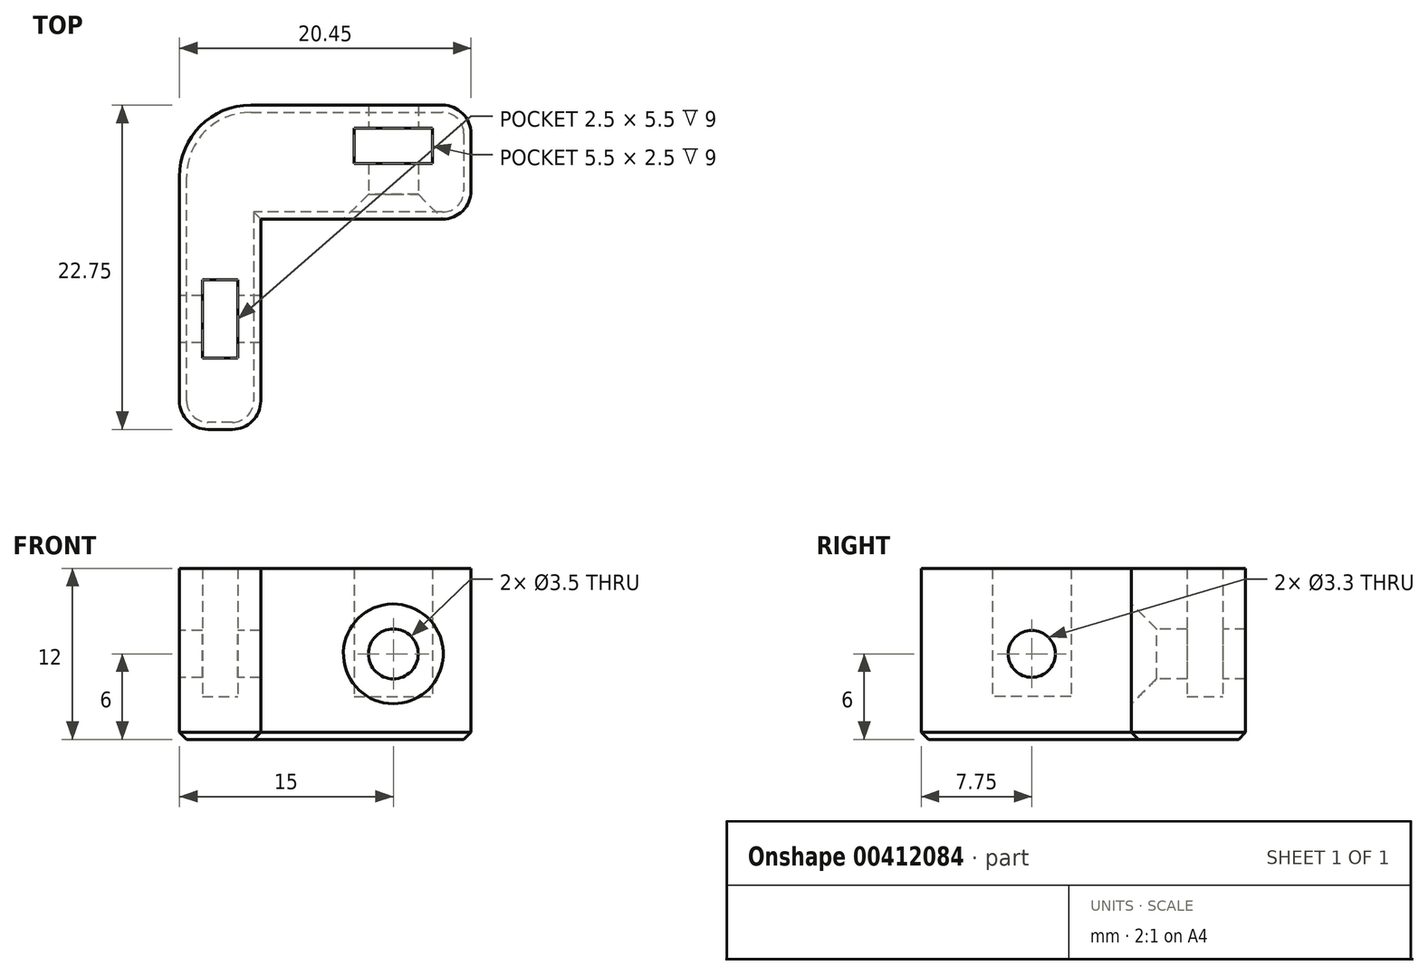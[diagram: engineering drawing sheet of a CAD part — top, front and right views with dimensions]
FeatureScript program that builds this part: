
annotation { "Feature Type Name" : "Feature", "Feature Type Description" : "" }
export const myFeature = defineFeature(function(context is Context, id is Id, definition is map)
    precondition{}
    {
        {
            var Q0;
            Q0=qCreatedBy(makeId("Top.planeOp"),FACE);
            var sketch = newSketch(context, id + "F0", { "sketchPlane" : qUnion([Q0])});
            skLineSegment(sketch, "E0", {"start": v(-15, -7.75) * mm, "end": v(-15, 15) * mm});
            skLineSegment(sketch, "E1", {"start": v(-15, 15) * mm, "end": v(5.45, 15) * mm});
            skLineSegment(sketch, "E2", {"start": v(5.45, 15) * mm, "end": v(5.45, 7) * mm});
            skLineSegment(sketch, "E3", {"start": v(5.45, 7) * mm, "end": v(-9.3, 7) * mm});
            skLineSegment(sketch, "E4", {"start": v(-9.3, 7) * mm, "end": v(-9.3, -7.75) * mm});
            skLineSegment(sketch, "E5", {"start": v(-9.3, -7.75) * mm, "end": v(-15, -7.75) * mm});
            skLineSegment(sketch, "E6.bottom", {"start": v(-13.4, 2.75) * mm, "end": v(-10.9, 2.75) * mm});
            skLineSegment(sketch, "E6.top", {"start": v(-13.4, -2.75) * mm, "end": v(-10.9, -2.75) * mm});
            skLineSegment(sketch, "E6.left", {"start": v(-13.4, 2.75) * mm, "end": v(-13.4, -2.75) * mm});
            skLineSegment(sketch, "E6.right", {"start": v(-10.9, 2.75) * mm, "end": v(-10.9, -2.75) * mm});
            skLineSegment(sketch, "E7.bottom", {"start": v(-2.75, 10.9) * mm, "end": v(2.75, 10.9) * mm});
            skLineSegment(sketch, "E7.top", {"start": v(-2.75, 13.4) * mm, "end": v(2.75, 13.4) * mm});
            skLineSegment(sketch, "E7.left", {"start": v(-2.75, 10.9) * mm, "end": v(-2.75, 13.4) * mm});
            skLineSegment(sketch, "E7.right", {"start": v(2.75, 10.9) * mm, "end": v(2.75, 13.4) * mm});
            skLineSegment(sketch, "E8", {"start": v(-10.9, 2.75) * mm, "end": v(-2.75, 10.9) * mm, "construction": true});
            skLineSegment(sketch, "E9.bottom", {"start": v(-15, 15) * mm, "end": v(-21, 15) * mm, "construction": true});
            skLineSegment(sketch, "E9.top", {"start": v(-15, -17.94) * mm, "end": v(-21, -17.94) * mm, "construction": true});
            skLineSegment(sketch, "E9.left", {"start": v(-15, 15) * mm, "end": v(-15, -17.94) * mm, "construction": true});
            skLineSegment(sketch, "E9.right", {"start": v(-21, 15) * mm, "end": v(-21, -17.94) * mm, "construction": true});
            skLineSegment(sketch, "E10.bottom", {"start": v(-21, 15) * mm, "end": v(24.07, 15) * mm, "construction": true});
            skLineSegment(sketch, "E10.top", {"start": v(-21, 21) * mm, "end": v(24.07, 21) * mm, "construction": true});
            skLineSegment(sketch, "E10.left", {"start": v(-21, 15) * mm, "end": v(-21, 21) * mm, "construction": true});
            skLineSegment(sketch, "E10.right", {"start": v(24.07, 15) * mm, "end": v(24.07, 21) * mm, "construction": true});
            skLineSegment(sketch, "E11", {"start": v(-9.3, -7.75) * mm, "end": v(5.45, 7) * mm, "construction": true});
            skSolve(sketch);
        }
        {
            var Q0;
            Q0=makeQuery(id+"F0.imprint","IMPRINT",FACE,{"disambiguationData":[TD([[makeQuery(id+"F0.imprint","IMPRINT",EDGE,{"derivedFrom":sQuery(id+"F0.wireOp",EDGE,"E0")}),-1.0]])]});
            extrude(context, id + "F1", {"entities" : qUnion([Q0]), "depth" : 6 * mm, "hasSecondDirection" : true, "secondDirectionOppositeDirection" : true, "secondDirectionDepth" : 6 * mm});
        }
        {
            var Q0;
            Q0=makeQuery(id+"F1.opExtrude","CAP_FACE",FACE,{"disambiguationData":[OSD([sQuery(id+"F0.wireOp",EDGE,"E0"),sQuery(id+"F0.wireOp",EDGE,"E1"),sQuery(id+"F0.wireOp",EDGE,"E2"),sQuery(id+"F0.wireOp",EDGE,"E3"),sQuery(id+"F0.wireOp",EDGE,"E4"),sQuery(id+"F0.wireOp",EDGE,"E5"),sQuery(id+"F0.wireOp",EDGE,"E6.bottom"),sQuery(id+"F0.wireOp",EDGE,"E6.top"),sQuery(id+"F0.wireOp",EDGE,"E6.left"),sQuery(id+"F0.wireOp",EDGE,"E6.right"),sQuery(id+"F0.wireOp",EDGE,"E7.bottom"),sQuery(id+"F0.wireOp",EDGE,"E7.top"),sQuery(id+"F0.wireOp",EDGE,"E7.left"),sQuery(id+"F0.wireOp",EDGE,"E7.right")])],"isStart":true});
            var sketch = newSketch(context, id + "F2", { "sketchPlane" : qUnion([Q0])});
            skSolve(sketch);
        }
        {
            var Q0;
            Q0=makeQuery(id+"F2.imprint","IMPRINT",FACE,{"disambiguationData":[TD([[makeQuery(id+"F2.imprint","IMPRINT",EDGE,{"derivedFrom":makeQuery(id+"F1.opExtrude","CAP_EDGE",EDGE,{"disambiguationData":[OSD([sQuery(id+"F0.wireOp",EDGE,"E6.bottom")])],"isStart":true})}),1.0]])]});
            var Q1;
            Q1=makeQuery(id+"F2.imprint","IMPRINT",FACE,{"disambiguationData":[TD([[makeQuery(id+"F2.imprint","IMPRINT",EDGE,{"derivedFrom":makeQuery(id+"F1.opExtrude","CAP_EDGE",EDGE,{"disambiguationData":[OSD([sQuery(id+"F0.wireOp",EDGE,"E7.bottom")])],"isStart":true})}),-1.0]])]});
            extrude(context, id + "F3", {"entities" : qUnion([Q0, Q1]), "operationType" : NewBodyOperationType.ADD, "oppositeDirection" : true, "depth" : 3 * mm});
        }
        {
            var Q0;
            Q0=makeQuery(id+"F1.opExtrude","SWEPT_FACE",FACE,{"disambiguationData":[OSD([sQuery(id+"F0.wireOp",EDGE,"E0")])]});
            var sketch = newSketch(context, id + "F4", { "sketchPlane" : qUnion([Q0])});
            skPoint(sketch, "E12", {"position": v(0, 0) * mm});
            skSolve(sketch);
        }
        {
            var Q0;
            Q0=makeQuery(id+"F1.opExtrude","SWEPT_FACE",FACE,{"disambiguationData":[OSD([sQuery(id+"F0.wireOp",EDGE,"E3")])]});
            var sketch = newSketch(context, id + "F5", { "sketchPlane" : qUnion([Q0])});
            skPoint(sketch, "E13", {"position": v(0, 0) * mm});
            skSolve(sketch);
        }
        {
            var Q0;
            Q0=sQuery(id+"F4.wireOp",VERTEX,"E12");
            var Q1;
            Q1=makeQuery(id+"F1.opExtrude","SWEPT_BODY",BODY,{"disambiguationData":[OSD([sQuery(id+"F0.wireOp",EDGE,"E0"),sQuery(id+"F0.wireOp",EDGE,"E1"),sQuery(id+"F0.wireOp",EDGE,"E2"),sQuery(id+"F0.wireOp",EDGE,"E3"),sQuery(id+"F0.wireOp",EDGE,"E4"),sQuery(id+"F0.wireOp",EDGE,"E5"),sQuery(id+"F0.wireOp",EDGE,"E6.bottom"),sQuery(id+"F0.wireOp",EDGE,"E6.top"),sQuery(id+"F0.wireOp",EDGE,"E6.left"),sQuery(id+"F0.wireOp",EDGE,"E6.right"),sQuery(id+"F0.wireOp",EDGE,"E7.bottom"),sQuery(id+"F0.wireOp",EDGE,"E7.top"),sQuery(id+"F0.wireOp",EDGE,"E7.left"),sQuery(id+"F0.wireOp",EDGE,"E7.right")])]});
            hole(context, id + "F6", {"style" : HoleStyle.SIMPLE, "endStyle" : HoleEndStyle.BLIND, "standardTappedOrClearance" : lookupTablePath({ "standard" : "ISO", "fit" : "Normal", "size" : "M3", "type" : "Clearance" }), "standardBlindInLast" : lookupTablePath({ "fit" : "Standard", "standard" : "ISO", "size" : "M3", "type" : "Clearance" }), "holeDiameter" : 3.3 * mm, "holeDepth" : 100 * mm, "isTappedThrough" : true, "tappedDepth" : 15 * mm, "tapClearance" : 0, "startFromSketch" : true, "locations" : qUnion([Q0]), "scope" : qUnion([Q1])});
        }
        {
            var Q0;
            Q0=sQuery(id+"F5.wireOp",VERTEX,"E13");
            var Q1;
            Q1=makeQuery(id+"F1.opExtrude","SWEPT_BODY",BODY,{"disambiguationData":[OSD([sQuery(id+"F0.wireOp",EDGE,"E0"),sQuery(id+"F0.wireOp",EDGE,"E1"),sQuery(id+"F0.wireOp",EDGE,"E2"),sQuery(id+"F0.wireOp",EDGE,"E3"),sQuery(id+"F0.wireOp",EDGE,"E4"),sQuery(id+"F0.wireOp",EDGE,"E5"),sQuery(id+"F0.wireOp",EDGE,"E6.bottom"),sQuery(id+"F0.wireOp",EDGE,"E6.top"),sQuery(id+"F0.wireOp",EDGE,"E6.left"),sQuery(id+"F0.wireOp",EDGE,"E6.right"),sQuery(id+"F0.wireOp",EDGE,"E7.bottom"),sQuery(id+"F0.wireOp",EDGE,"E7.top"),sQuery(id+"F0.wireOp",EDGE,"E7.left"),sQuery(id+"F0.wireOp",EDGE,"E7.right")])]});
            hole(context, id + "F7", {"style" : HoleStyle.C_SINK, "endStyle" : HoleEndStyle.BLIND, "holeDiameter" : 3.5 * mm, "cSinkDiameter" : 7 * mm, "cSinkAngle" : 90 * degree, "holeDepth" : 100 * mm, "isTappedThrough" : true, "tappedDepth" : 15 * mm, "tapClearance" : 0, "startFromSketch" : true, "locations" : qUnion([Q0]), "scope" : qUnion([Q1])});
        }
        {
            var Q0;
            Q0=makeQuery(id+"F1.opExtrude","SWEPT_EDGE",EDGE,{"disambiguationData":[OSD([sQuery(id+"F0.wireOp",EDGE,"E0"),sQuery(id+"F0.wireOp",EDGE,"E1")])]});
            fillet(context, id + "F8", {"entities" : qUnion([Q0]), "radius" : 5 * mm, "tangentPropagation" : true, "allowEdgeOverflow" : false});
        }
        {
            var Q0;
            Q0=makeQuery(id+"F1.opExtrude","SWEPT_EDGE",EDGE,{"disambiguationData":[OSD([sQuery(id+"F0.wireOp",EDGE,"E0"),sQuery(id+"F0.wireOp",EDGE,"E5")])]});
            var Q1;
            Q1=makeQuery(id+"F1.opExtrude","SWEPT_EDGE",EDGE,{"disambiguationData":[OSD([sQuery(id+"F0.wireOp",EDGE,"E4"),sQuery(id+"F0.wireOp",EDGE,"E5")])]});
            var Q2;
            Q2=makeQuery(id+"F1.opExtrude","SWEPT_EDGE",EDGE,{"disambiguationData":[OSD([sQuery(id+"F0.wireOp",EDGE,"E2"),sQuery(id+"F0.wireOp",EDGE,"E3")])]});
            var Q3;
            Q3=makeQuery(id+"F1.opExtrude","SWEPT_EDGE",EDGE,{"disambiguationData":[OSD([sQuery(id+"F0.wireOp",EDGE,"E1"),sQuery(id+"F0.wireOp",EDGE,"E2")])]});
            fillet(context, id + "F9", {"entities" : qUnion([Q0, Q1, Q2, Q3]), "radius" : 2 * mm, "tangentPropagation" : true, "allowEdgeOverflow" : false});
        }
        {
            var Q0;
            {var subQ0=sQuery(id+"F0.wireOp",EDGE,"E7.right");var subQ1=sQuery(id+"F0.wireOp",EDGE,"E7.left");var subQ2=sQuery(id+"F0.wireOp",EDGE,"E7.top");var subQ3=sQuery(id+"F0.wireOp",EDGE,"E7.bottom");var subQ4=sQuery(id+"F0.wireOp",EDGE,"E6.right");var subQ5=sQuery(id+"F0.wireOp",EDGE,"E6.left");var subQ6=sQuery(id+"F0.wireOp",EDGE,"E6.top");var subQ7=sQuery(id+"F0.wireOp",EDGE,"E6.bottom");Q0=makeQuery(id+"F3.boolean.opBoolean","MERGE",FACE,{"derivedFrom":[makeQuery(id+"F1.opExtrude","CAP_FACE",FACE,{"disambiguationData":[OSD([sQuery(id+"F0.wireOp",EDGE,"E0"),sQuery(id+"F0.wireOp",EDGE,"E1"),sQuery(id+"F0.wireOp",EDGE,"E2"),sQuery(id+"F0.wireOp",EDGE,"E3"),sQuery(id+"F0.wireOp",EDGE,"E4"),sQuery(id+"F0.wireOp",EDGE,"E5"),subQ7,subQ6,subQ5,subQ4,subQ3,subQ2,subQ1,subQ0])],"isStart":true}),makeQuery(id+"F3.opExtrude","CAP_FACE",FACE,{"disambiguationData":[OSD([subQ7,subQ6,subQ5,subQ4])],"isStart":true}),makeQuery(id+"F3.opExtrude","CAP_FACE",FACE,{"disambiguationData":[OSD([subQ3,subQ2,subQ1,subQ0])],"isStart":true})]});}
            chamfer(context, id + "F10", {"entities" : qUnion([Q0]), "width" : .5 * mm, "tangentPropagation" : true});
        }
    });
